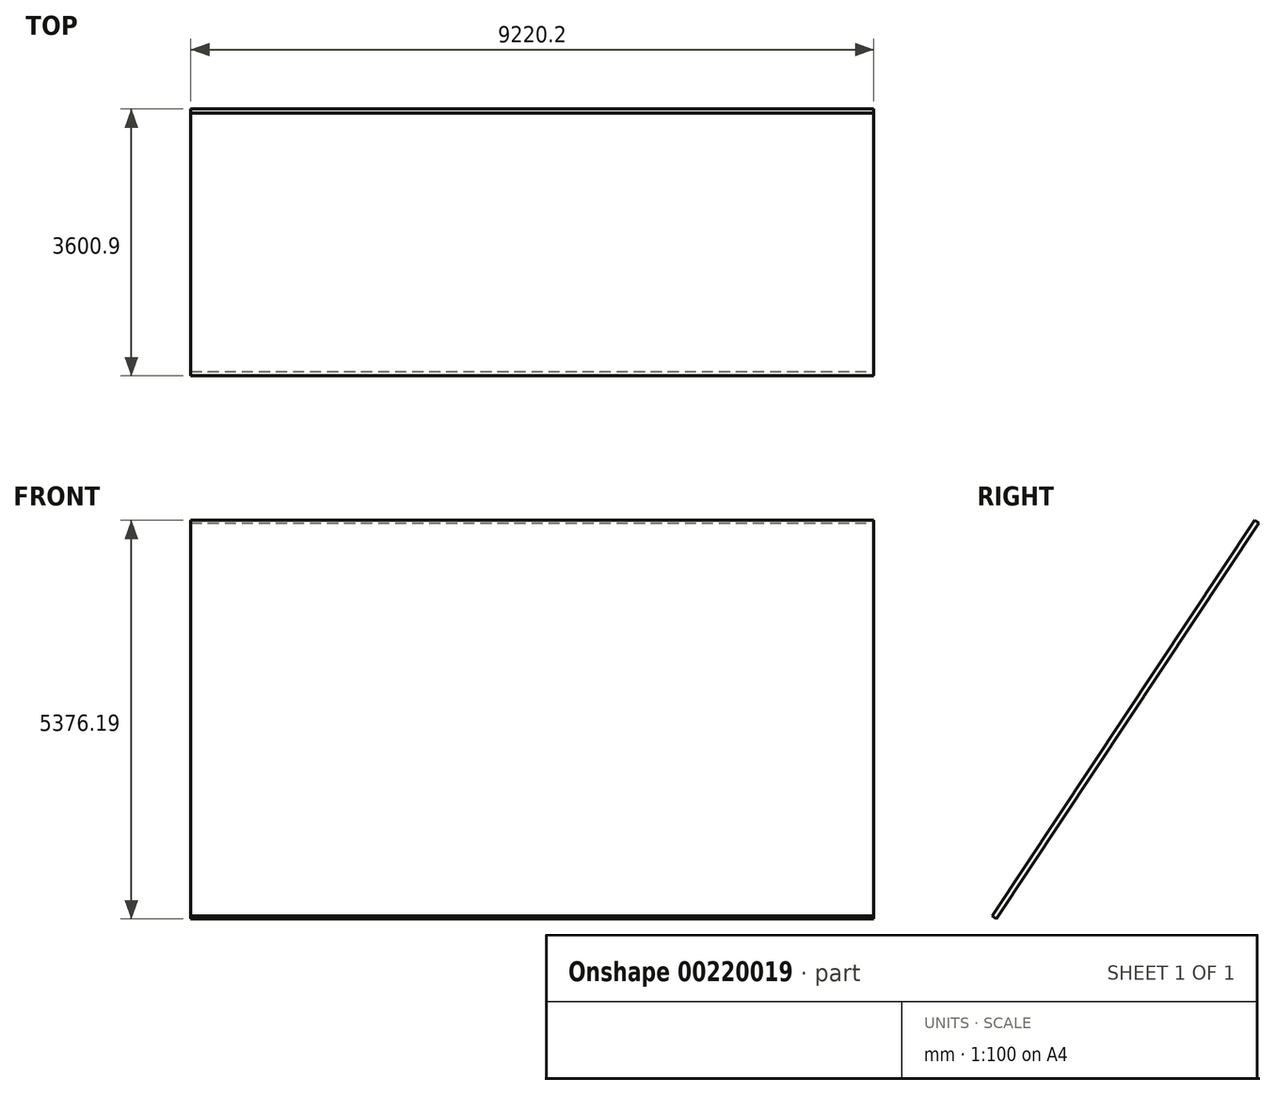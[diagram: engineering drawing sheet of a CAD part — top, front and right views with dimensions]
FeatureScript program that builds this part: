
annotation { "Feature Type Name" : "Feature", "Feature Type Description" : "" }
export const myFeature = defineFeature(function(context is Context, id is Id, definition is map)
    precondition{}
    {
        {
            var Q0;
            Q0=qCreatedBy(makeId("Right.planeOp"),FACE);
            var sketch = newSketch(context, id + "F0", { "sketchPlane" : qUnion([Q0])});
            skLineSegment(sketch, "E0", {"start": v(0, 10515.6) * mm, "end": v(-2933.7, 6096) * mm});
            skLineSegment(sketch, "E1", {"start": v(-2933.7, 6096) * mm, "end": v(-3543.3, 5177.64) * mm});
            skSolve(sketch);
        }
        {
            var Q0;
            Q0=sQuery(id+"F0.wireOp",EDGE,"E1");
            var Q1;
            Q1=sQuery(id+"F0.wireOp",EDGE,"E0");
            extrude(context, id + "F1", {"bodyType" : ToolBodyType.SURFACE, "surfaceEntities" : qUnion([Q0, Q1]), "endBound" : BoundingType.SYMMETRIC, "depth" : 9220.2 * mm});
        }
        {
            var Q0;
            Q0=makeQuery(id+"F1.opExtrude","SWEPT_FACE",FACE,{"disambiguationData":[OSD([sQuery(id+"F0.wireOp",EDGE,"E0"),sQuery(id+"F0.wireOp",EDGE,"E1")])]});
            extrude(context, id + "F2", {"entities" : qUnion([Q0]), "depth" : 69.14 * mm});
        }
    });
